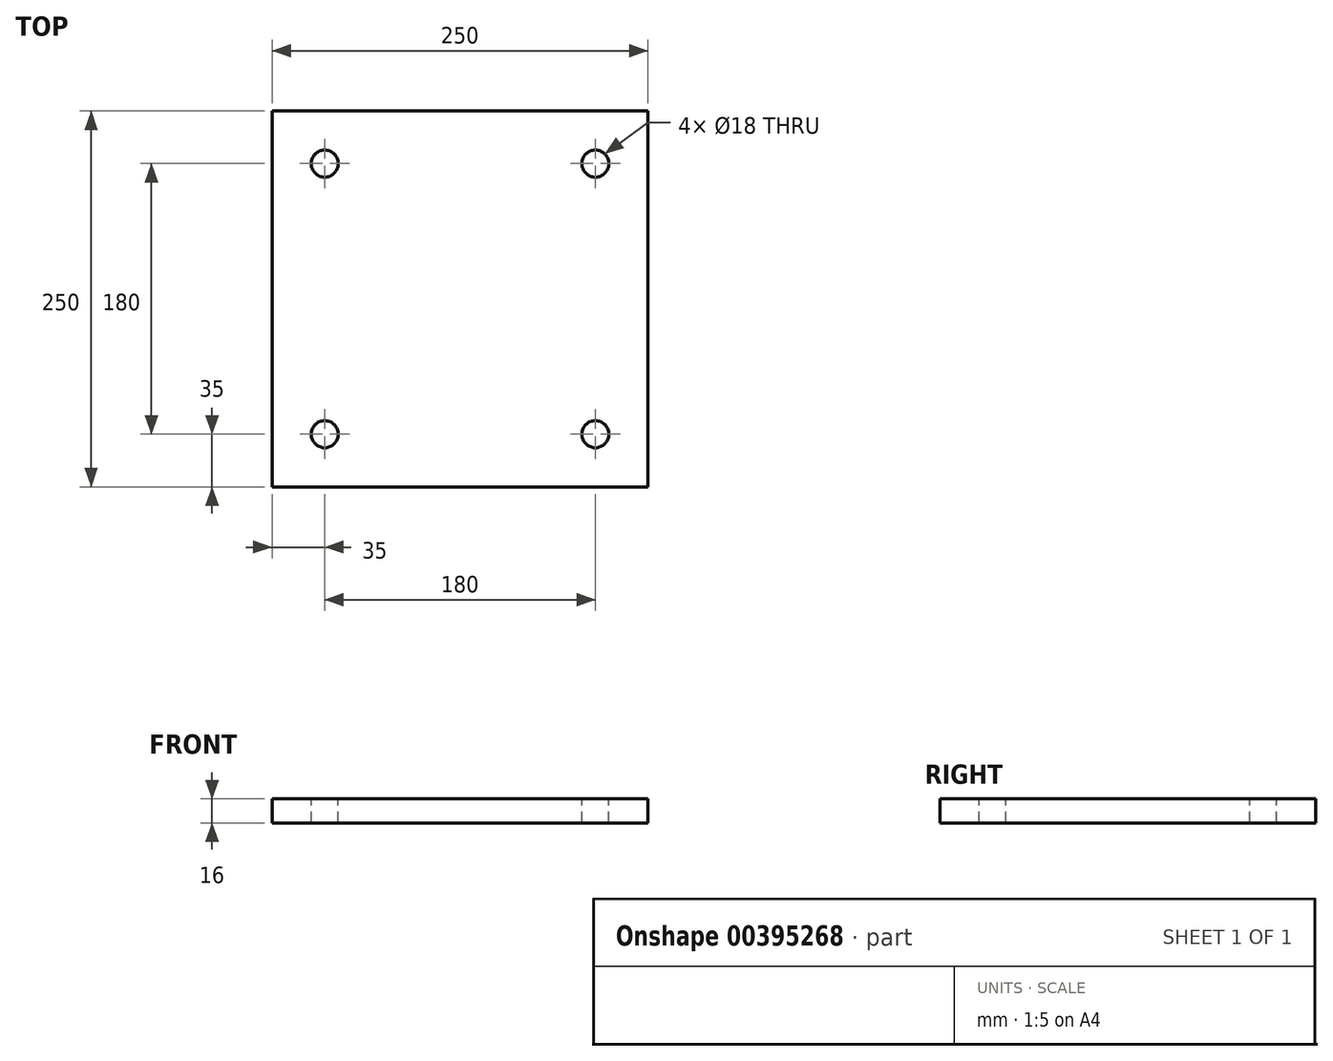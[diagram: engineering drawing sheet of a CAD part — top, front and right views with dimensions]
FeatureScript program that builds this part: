
annotation { "Feature Type Name" : "Feature", "Feature Type Description" : "" }
export const myFeature = defineFeature(function(context is Context, id is Id, definition is map)
    precondition{}
    {
        {
            var Q0;
            Q0=qCreatedBy(makeId("Top.planeOp"),FACE);
            var sketch = newSketch(context, id + "F0", { "sketchPlane" : qUnion([Q0])});
            skLineSegment(sketch, "E0.bottom", {"start": v(125, 125) * mm, "end": v(-125, 125) * mm});
            skLineSegment(sketch, "E0.top", {"start": v(125, -125) * mm, "end": v(-125, -125) * mm});
            skLineSegment(sketch, "E0.left", {"start": v(125, 125) * mm, "end": v(125, -125) * mm});
            skLineSegment(sketch, "E0.right", {"start": v(-125, 125) * mm, "end": v(-125, -125) * mm});
            skPoint(sketch, "E0.middle", {"position": v(0, 0) * mm});
            skSolve(sketch);
        }
        {
            var Q0;
            Q0 = qSketchRegion(id + "F0", true);
            extrude(context, id + "F1", {"entities" : qUnion([Q0]), "depth" : 16 * mm});
        }
        {
            var Q0;
            Q0=makeQuery(id+"F1.opExtrude","CAP_FACE",FACE,{"disambiguationData":[OSD([sQuery(id+"F0.wireOp",EDGE,"E0.bottom"),sQuery(id+"F0.wireOp",EDGE,"E0.top"),sQuery(id+"F0.wireOp",EDGE,"E0.left"),sQuery(id+"F0.wireOp",EDGE,"E0.right")])],"isStart":false});
            var sketch = newSketch(context, id + "F2", { "sketchPlane" : qUnion([Q0])});
            skPoint(sketch, "E1", {"position": v(-90, 90) * mm});
            skPoint(sketch, "E2", {"position": v(90, 90) * mm});
            skPoint(sketch, "E3", {"position": v(90, -90) * mm});
            skPoint(sketch, "E4", {"position": v(-90, -90) * mm});
            skSolve(sketch);
        }
        {
            var Q0;
            Q0=sQuery(id+"F2.wireOp",VERTEX,"E1");
            var Q1;
            Q1=sQuery(id+"F2.wireOp",VERTEX,"E2");
            var Q2;
            Q2=sQuery(id+"F2.wireOp",VERTEX,"E3");
            var Q3;
            Q3=sQuery(id+"F2.wireOp",VERTEX,"E4");
            var Q4;
            Q4=makeQuery(id+"F1.opExtrude","SWEPT_BODY",BODY,{"disambiguationData":[OSD([sQuery(id+"F0.wireOp",EDGE,"E0.bottom"),sQuery(id+"F0.wireOp",EDGE,"E0.top"),sQuery(id+"F0.wireOp",EDGE,"E0.left"),sQuery(id+"F0.wireOp",EDGE,"E0.right")])]});
            hole(context, id + "F3", {"style" : HoleStyle.SIMPLE, "endStyle" : HoleEndStyle.BLIND, "holeDiameter" : 18 * mm, "holeDepth" : 20 * mm, "isTappedThrough" : true, "tappedDepth" : 12 * mm, "tapClearance" : 3, "startFromSketch" : true, "locations" : qUnion([Q0, Q1, Q2, Q3]), "scope" : qUnion([Q4])});
        }
    });
